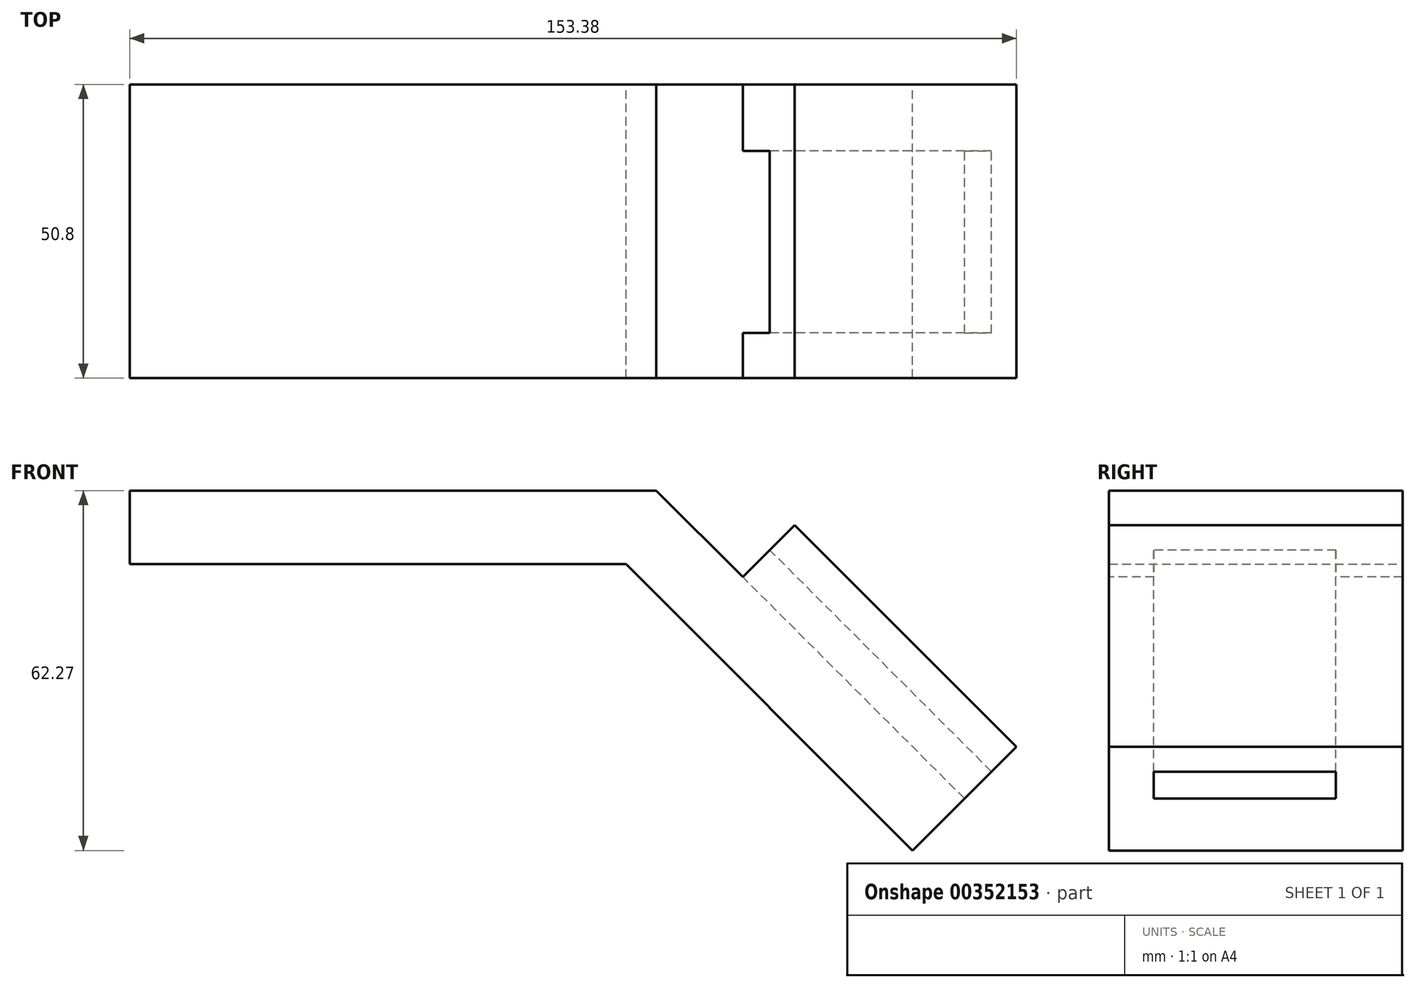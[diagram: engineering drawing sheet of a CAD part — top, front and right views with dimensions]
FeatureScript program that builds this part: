
annotation { "Feature Type Name" : "Feature", "Feature Type Description" : "" }
export const myFeature = defineFeature(function(context is Context, id is Id, definition is map)
    precondition{}
    {
        {
            var Q0;
            Q0=qCreatedBy(makeId("Front.planeOp"),FACE);
            var sketch = newSketch(context, id + "F0", { "sketchPlane" : qUnion([Q0])});
            skLineSegment(sketch, "E0.bottom", {"start": v(0, 0) * mm, "end": v(85.85, 0) * mm});
            skLineSegment(sketch, "E0.top", {"start": v(0, -12.7) * mm, "end": v(85.85, -12.7) * mm});
            skLineSegment(sketch, "E0.left", {"start": v(0, 0) * mm, "end": v(0, -12.7) * mm});
            skLineSegment(sketch, "E0.right", {"start": v(85.85, 0) * mm, "end": v(85.85, -12.7) * mm});
            skLineSegment(sketch, "E1.bottom", {"start": v(94.83, -3.72) * mm, "end": v(144.4, -53.3) * mm});
            skLineSegment(sketch, "E1.top", {"start": v(85.85, -12.7) * mm, "end": v(135.42, -62.27) * mm});
            skLineSegment(sketch, "E1.left", {"start": v(94.83, -3.72) * mm, "end": v(85.85, -12.7) * mm});
            skLineSegment(sketch, "E1.right", {"start": v(144.4, -53.3) * mm, "end": v(135.42, -62.27) * mm});
            skLineSegment(sketch, "E2", {"start": v(85.85, 0) * mm, "end": v(91.11, 0) * mm});
            skLineSegment(sketch, "E3", {"start": v(94.83, -3.72) * mm, "end": v(91.11, 0) * mm});
            skSolve(sketch);
        }
        {
            var Q0;
            Q0 = qSketchRegion(id + "F0", true);
            extrude(context, id + "F1", {"entities" : qUnion([Q0]), "depth" : 50.8 * mm});
        }
        {
            var Q0;
            Q0=makeQuery(id+"F1.opExtrude","CAP_FACE",FACE,{"disambiguationData":[OSD([sQuery(id+"F0.wireOp",EDGE,"E0.bottom"),sQuery(id+"F0.wireOp",EDGE,"E0.top"),sQuery(id+"F0.wireOp",EDGE,"E0.left"),sQuery(id+"F0.wireOp",EDGE,"E1.bottom"),sQuery(id+"F0.wireOp",EDGE,"E1.top"),sQuery(id+"F0.wireOp",EDGE,"E1.right"),sQuery(id+"F0.wireOp",EDGE,"E2"),sQuery(id+"F0.wireOp",EDGE,"E3")])],"isStart":false});
            var sketch = newSketch(context, id + "F2", { "sketchPlane" : qUnion([Q0])});
            skLineSegment(sketch, "E4.bottom", {"start": v(144.4, -53.3) * mm, "end": v(106.06, -14.95) * mm});
            skLineSegment(sketch, "E4.top", {"start": v(153.38, -44.31) * mm, "end": v(115.04, -5.96) * mm});
            skLineSegment(sketch, "E4.left", {"start": v(144.4, -53.3) * mm, "end": v(153.38, -44.31) * mm});
            skLineSegment(sketch, "E4.right", {"start": v(106.06, -14.95) * mm, "end": v(115.04, -5.96) * mm});
            skSolve(sketch);
        }
        {
            var Q0;
            Q0 = qSketchRegion(id + "F2", true);
            extrude(context, id + "F3", {"entities" : qUnion([Q0]), "operationType" : NewBodyOperationType.ADD, "oppositeDirection" : true, "depth" : 50.8 * mm});
        }
        {
            var Q0;
            Q0=makeQuery(id+"F3.opExtrude","SWEPT_FACE",FACE,{"disambiguationData":[OSD([sQuery(id+"F2.wireOp",EDGE,"E4.top")])]});
            var sketch = newSketch(context, id + "F4", { "sketchPlane" : qUnion([Q0])});
            skLineSegment(sketch, "E5", {"start": v(139.8, -25.4) * mm, "end": v(85.94, -25.4) * mm});
            skArc(sketch, "E6", {"start": v(133.42, -50.8) * mm, "mid": v(139.8, -25.4) * mm, "end": v(133.42, 0) * mm});
            skLineSegment(sketch, "E7", {"start": v(139.8, -50.8) * mm, "end": v(133.42, -50.8) * mm});
            skLineSegment(sketch, "E8", {"start": v(139.8, 0) * mm, "end": v(133.42, 0) * mm});
            skLineSegment(sketch, "E9", {"start": v(139.8, 0) * mm, "end": v(139.8, -50.8) * mm});
            skSolve(sketch);
        }
        {
            var Q0;
            Q0 = qSketchRegion(id + "F4", true);
            extrude(context, id + "F5", {"entities" : qUnion([Q0]), "operationType" : NewBodyOperationType.REMOVE, "endBound" : BoundingType.THROUGH_ALL, "oppositeDirection" : true, "depth" : 25.4 * mm});
        }
        {
            var Q0;
            Q0=makeQuery(id+"F3.opExtrude","SWEPT_FACE",FACE,{"disambiguationData":[OSD([sQuery(id+"F2.wireOp",EDGE,"E4.top")])]});
            var sketch = newSketch(context, id + "F6", { "sketchPlane" : qUnion([Q0])});
            skLineSegment(sketch, "E10", {"start": v(139.8, -25.4) * mm, "end": v(85.94, -25.4) * mm});
            skLineSegment(sketch, "E11.bottom", {"start": v(85.56, -35.05) * mm, "end": v(145.25, -35.05) * mm});
            skLineSegment(sketch, "E11.top", {"start": v(85.56, -15.75) * mm, "end": v(145.25, -15.75) * mm});
            skLineSegment(sketch, "E11.left", {"start": v(85.56, -35.05) * mm, "end": v(85.56, -15.75) * mm});
            skLineSegment(sketch, "E11.right", {"start": v(145.25, -35.05) * mm, "end": v(145.25, -15.75) * mm});
            skSolve(sketch);
        }
        {
            var Q0;
            Q0 = qSketchRegion(id + "F6", true);
            extrude(context, id + "F7", {"entities" : qUnion([Q0]), "operationType" : NewBodyOperationType.REMOVE, "oppositeDirection" : true, "depth" : 6.1 * mm});
        }
        {
            var Q0;
            Q0=makeQuery(id+"F3.opExtrude","SWEPT_FACE",FACE,{"disambiguationData":[OSD([sQuery(id+"F2.wireOp",EDGE,"E4.right")])]});
            var sketch = newSketch(context, id + "F8", { "sketchPlane" : qUnion([Q0])});
            skLineSegment(sketch, "E12.bottom", {"start": v(11.53, 71.03) * mm, "end": v(43.02, 71.03) * mm});
            skLineSegment(sketch, "E12.top", {"start": v(11.53, 64.43) * mm, "end": v(43.02, 64.43) * mm});
            skLineSegment(sketch, "E12.left", {"start": v(11.53, 71.03) * mm, "end": v(11.53, 64.43) * mm});
            skLineSegment(sketch, "E12.right", {"start": v(43.02, 71.03) * mm, "end": v(43.02, 64.43) * mm});
            skSolve(sketch);
        }
        {
            var Q0;
            Q0 = qSketchRegion(id + "F8", true);
            extrude(context, id + "F9", {"entities" : qUnion([Q0]), "operationType" : NewBodyOperationType.REMOVE, "endBound" : BoundingType.THROUGH_ALL, "oppositeDirection" : true, "depth" : 25.4 * mm});
        }
    });
